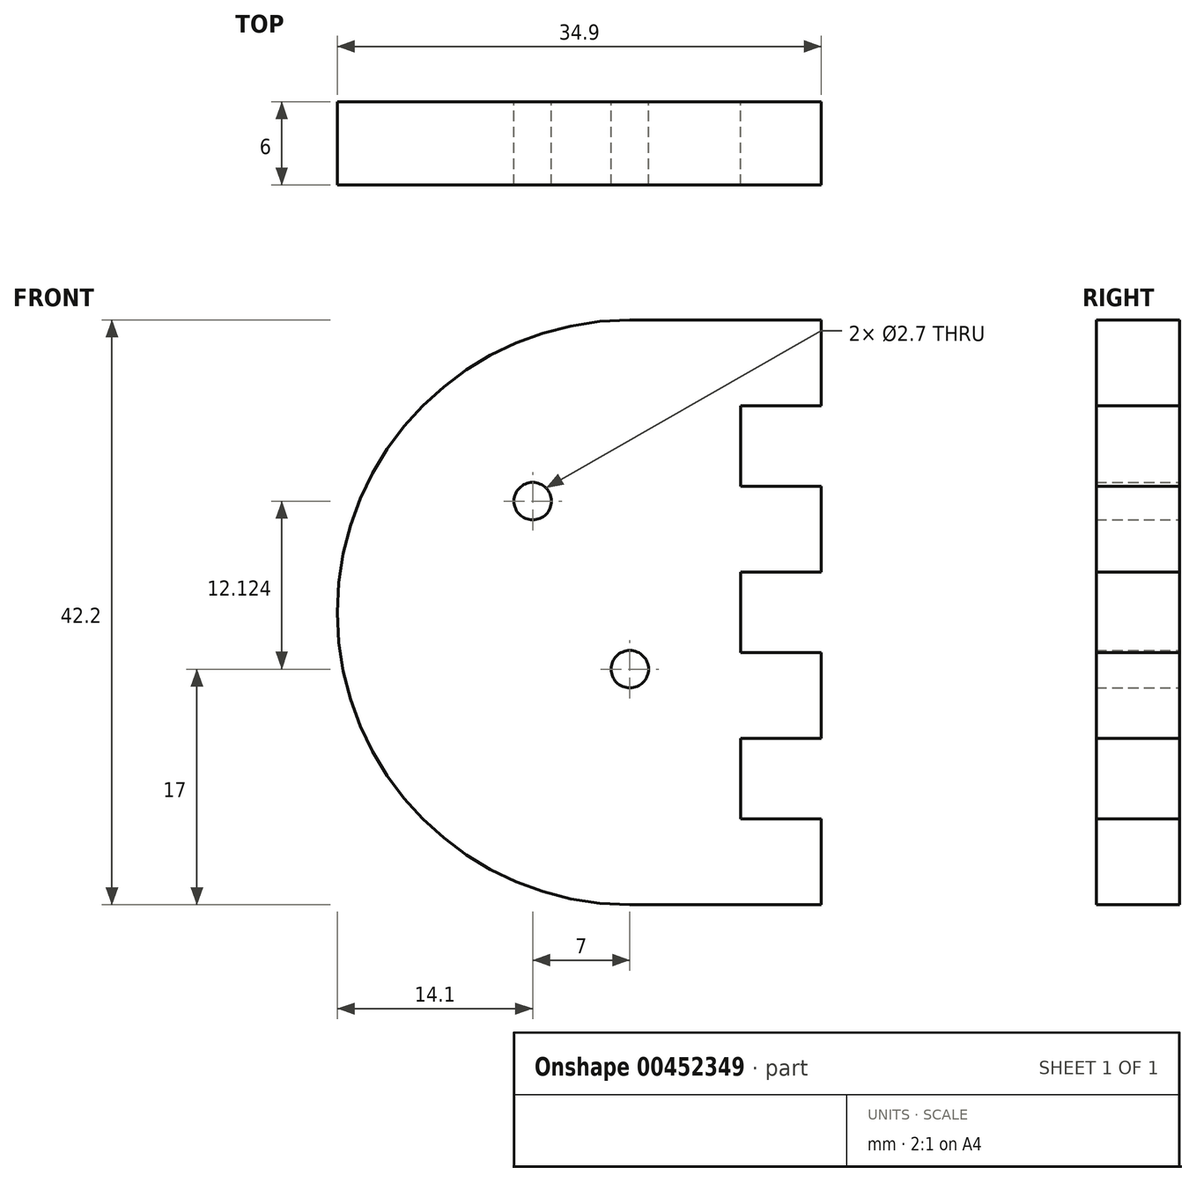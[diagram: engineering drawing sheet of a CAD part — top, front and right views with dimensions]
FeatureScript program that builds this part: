
annotation { "Feature Type Name" : "Feature", "Feature Type Description" : "" }
export const myFeature = defineFeature(function(context is Context, id is Id, definition is map)
    precondition{}
    {
        {
            var Q0;
            Q0=qCreatedBy(makeId("Front.planeOp"),FACE);
            var sketch = newSketch(context, id + "F0", { "sketchPlane" : qUnion([Q0])});
            skLineSegment(sketch, "E0.top", {"start": v(0, -17) * mm, "end": v(13.8, -17) * mm});
            skCircle(sketch, "E1", {"center": v(0, 0) * mm, "radius": 1.35 * mm});
            skLineSegment(sketch, "E2", {"start": v(13.8, -17) * mm, "end": v(13.8, -10.8) * mm});
            skLineSegment(sketch, "E3", {"start": v(13.8, -10.8) * mm, "end": v(8, -10.8) * mm});
            skLineSegment(sketch, "E4", {"start": v(8, -10.8) * mm, "end": v(8, -5) * mm});
            skLineSegment(sketch, "E5", {"start": v(8, -5) * mm, "end": v(13.8, -5) * mm});
            skLineSegment(sketch, "E6", {"start": v(13.8, -5) * mm, "end": v(13.8, 1.2) * mm});
            skLineSegment(sketch, "E7", {"start": v(13.8, 1.2) * mm, "end": v(8, 1.2) * mm});
            skLineSegment(sketch, "E8", {"start": v(8, 1.2) * mm, "end": v(8, 7) * mm});
            skLineSegment(sketch, "E9", {"start": v(8, 7) * mm, "end": v(13.8, 7) * mm});
            skLineSegment(sketch, "E10", {"start": v(13.8, 7) * mm, "end": v(13.8, 13.2) * mm});
            skLineSegment(sketch, "E11", {"start": v(13.8, 13.2) * mm, "end": v(8, 13.2) * mm});
            skLineSegment(sketch, "E12", {"start": v(8, 13.2) * mm, "end": v(8, 19) * mm});
            skLineSegment(sketch, "E13", {"start": v(8, 19) * mm, "end": v(13.8, 19) * mm});
            skLineSegment(sketch, "E14", {"start": v(13.8, 19) * mm, "end": v(13.8, 25.2) * mm});
            skLineSegment(sketch, "E15", {"start": v(13.8, 25.2) * mm, "end": v(0, 25.2) * mm});
            skArc(sketch, "E16", {"start": v(0, 25.2) * mm, "mid": v(-21.1, 4.1) * mm, "end": v(0, -17) * mm});
            skLineSegment(sketch, "E17", {"start": v(0, 0) * mm, "end": v(-7, 12.12) * mm, "construction": true});
            skCircle(sketch, "E18", {"center": v(-7, 12.12) * mm, "radius": 1.35 * mm});
            skSolve(sketch);
        }
        {
            var Q0;
            Q0 = qSketchRegion(id + "F0", true);
            extrude(context, id + "F1", {"entities" : qUnion([Q0]), "depth" : 6 * mm});
        }
    });
